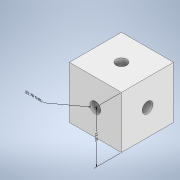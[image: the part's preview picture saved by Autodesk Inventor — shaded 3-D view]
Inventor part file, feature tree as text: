
AUTODESK INVENTOR PART (.ipt)
format: ipt  version: 2022 (Build 260153000, 153)  size: 131,584 bytes
history: native  units: mm
features: extrude x4, sketch x4, other x2, hole x1
ambient origin geometry x8: Origin, YZ Plane, XZ Plane, XY Plane, X Axis, Y Axis, Z Axis, Center Point
bodies: Solid1 (feature_tree)
feature tree (11):
  other  "Annotations"
  extrude  "Extrusion1"  Depth=13.2mm TaperAngle=0.0deg
  sketch  "Sketch2"  dims[d3=2.7mm d4=2.7mm]
  sketch  "Sketch3"  dims[d5=2.7mm d6=0.0mm d7=0.0mm]
  extrude  "Extrusion2"  Depth=2.7mm
  extrude  "Extrusion3"  TaperAngle=0.0deg  [1 undecoded]
  extrude  "Extrusion4"  TaperAngle=0.0deg  [1 undecoded]
  sketch  "Sketch1"  dims[d0=13.2mm d1=13.2mm d2=0.0mm]
  sketch  "Sketch4"  dims[d8=0.0mm d9=0.0mm d10=0.0mm d11=0.0mm d12=38.588838mm d14=0.0mm d15=10.0mm d16=13.2mm]
  hole  "Hole Note 1"  [1 undecoded]
  other  "Linear Dimension 1"
note: 3 required parameter values undecoded (feature->parameter linkage not recoverable at this tier; creation-order binding heuristic only, values carry confidence <= 0.55)
